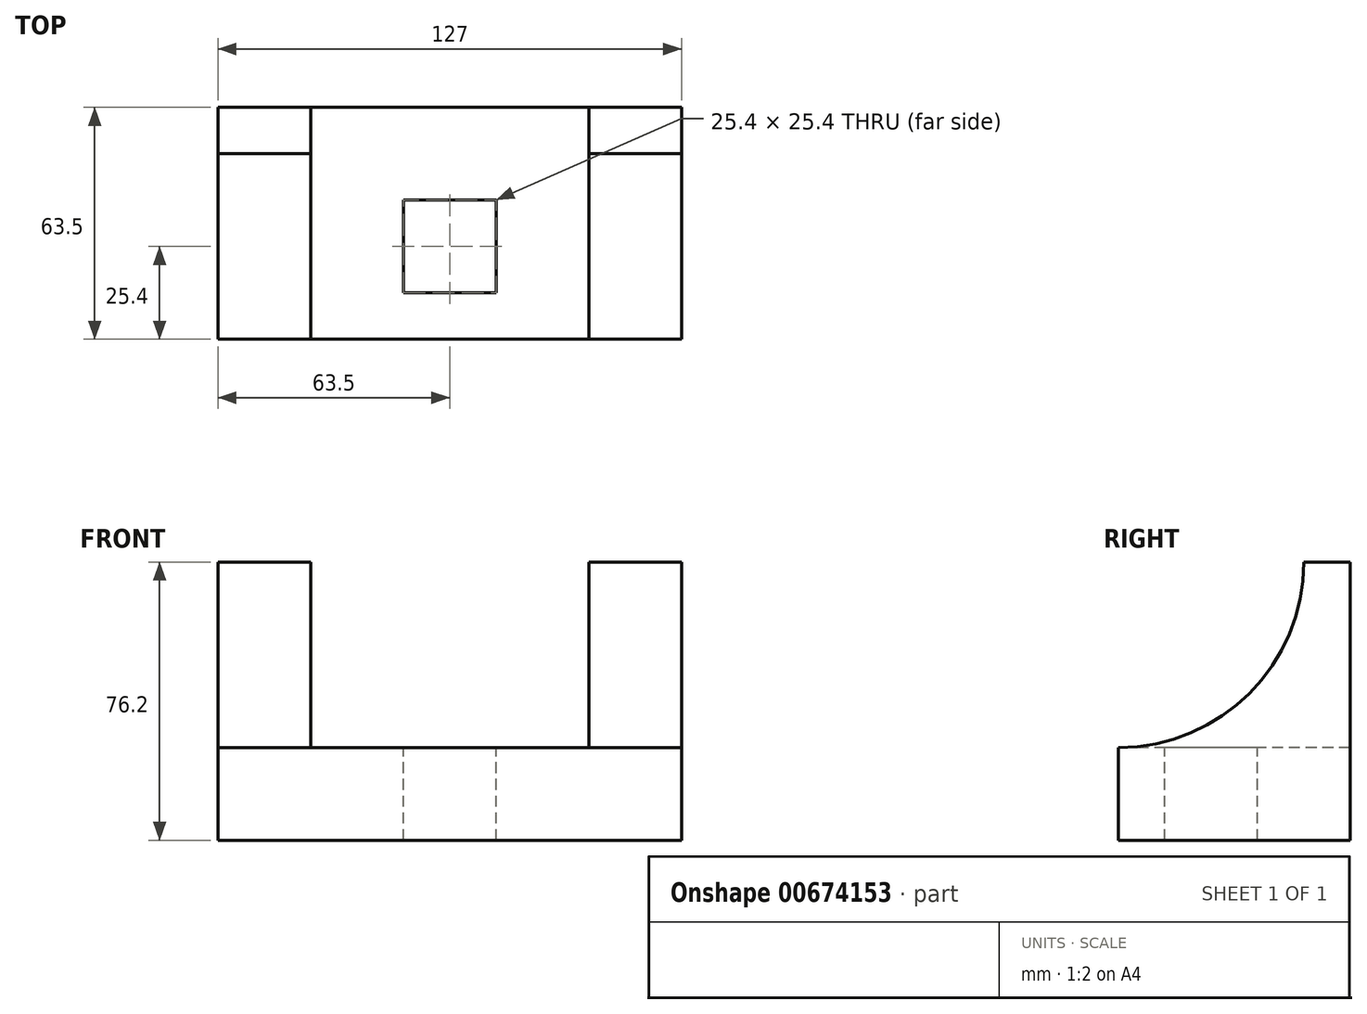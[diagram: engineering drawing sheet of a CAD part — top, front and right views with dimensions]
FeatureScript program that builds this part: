
annotation { "Feature Type Name" : "Feature", "Feature Type Description" : "" }
export const myFeature = defineFeature(function(context is Context, id is Id, definition is map)
    precondition{}
    {
        {
            var Q0;
            Q0=qCreatedBy(makeId("Front.planeOp"),FACE);
            var sketch = newSketch(context, id + "F0", { "sketchPlane" : qUnion([Q0])});
            skLineSegment(sketch, "E0.bottom", {"start": v(63.5, -38.1) * mm, "end": v(-63.5, -38.1) * mm});
            skLineSegment(sketch, "E0.top", {"start": v(63.5, 38.1) * mm, "end": v(-63.5, 38.1) * mm});
            skLineSegment(sketch, "E0.left", {"start": v(63.5, -38.1) * mm, "end": v(63.5, 38.1) * mm});
            skLineSegment(sketch, "E0.right", {"start": v(-63.5, -38.1) * mm, "end": v(-63.5, 38.1) * mm});
            skPoint(sketch, "E0.middle", {"position": v(0, 0) * mm});
            skSolve(sketch);
        }
        {
            var Q0;
            Q0 = qSketchRegion(id + "F0", true);
            extrude(context, id + "F1", {"entities" : qUnion([Q0]), "depth" : 63.5 * mm, "offsetDistance" : 25.4 * mm});
        }
        {
            var Q0;
            Q0=makeQuery(id+"F1.opExtrude","CAP_FACE",FACE,{"disambiguationData":[OSD([sQuery(id+"F0.wireOp",EDGE,"E0.bottom"),sQuery(id+"F0.wireOp",EDGE,"E0.top"),sQuery(id+"F0.wireOp",EDGE,"E0.left"),sQuery(id+"F0.wireOp",EDGE,"E0.right")])],"isStart":false});
            var sketch = newSketch(context, id + "F2", { "sketchPlane" : qUnion([Q0])});
            skLineSegment(sketch, "E1.bottom", {"start": v(-38.1, 38.1) * mm, "end": v(38.1, 38.1) * mm});
            skLineSegment(sketch, "E1.top", {"start": v(-38.1, -12.7) * mm, "end": v(38.1, -12.7) * mm});
            skLineSegment(sketch, "E1.left", {"start": v(-38.1, 38.1) * mm, "end": v(-38.1, -12.7) * mm});
            skLineSegment(sketch, "E1.right", {"start": v(38.1, 38.1) * mm, "end": v(38.1, -12.7) * mm});
            skSolve(sketch);
        }
        {
            var Q0;
            Q0 = qSketchRegion(id + "F2", true);
            extrude(context, id + "F3", {"entities" : qUnion([Q0]), "operationType" : NewBodyOperationType.REMOVE, "oppositeDirection" : true, "depth" : 63.5 * mm, "offsetDistance" : 25.4 * mm});
        }
        {
            var Q0;
            Q0=makeQuery(id+"F1.opExtrude","SWEPT_FACE",FACE,{"disambiguationData":[OSD([sQuery(id+"F0.wireOp",EDGE,"E0.right")])]});
            var sketch = newSketch(context, id + "F4", { "sketchPlane" : qUnion([Q0])});
            skCircle(sketch, "E2", {"center": v(63.5, 38.1) * mm, "radius": 50.8 * mm});
            skSolve(sketch);
        }
        {
            var Q0;
            Q0 = qSketchRegion(id + "F4", true);
            extrude(context, id + "F5", {"entities" : qUnion([Q0]), "operationType" : NewBodyOperationType.REMOVE, "oppositeDirection" : true, "depth" : 132.08 * mm, "offsetDistance" : 25.4 * mm});
        }
        {
            var Q0;
            Q0=makeQuery(id+"F3.boolean.opBoolean","COPY",FACE,{"derivedFrom":makeQuery(id+"F3.opExtrude","SWEPT_FACE",FACE,{"disambiguationData":[OSD([sQuery(id+"F2.wireOp",EDGE,"E1.top")])]})});
            var sketch = newSketch(context, id + "F6", { "sketchPlane" : qUnion([Q0])});
            skLineSegment(sketch, "E3.bottom", {"start": v(-12.7, -25.4) * mm, "end": v(12.7, -25.4) * mm});
            skLineSegment(sketch, "E3.top", {"start": v(-12.7, -50.8) * mm, "end": v(12.7, -50.8) * mm});
            skLineSegment(sketch, "E3.left", {"start": v(-12.7, -25.4) * mm, "end": v(-12.7, -50.8) * mm});
            skLineSegment(sketch, "E3.right", {"start": v(12.7, -25.4) * mm, "end": v(12.7, -50.8) * mm});
            skSolve(sketch);
        }
        {
            var Q0;
            Q0 = qSketchRegion(id + "F6", true);
            extrude(context, id + "F7", {"entities" : qUnion([Q0]), "operationType" : NewBodyOperationType.REMOVE, "oppositeDirection" : true, "depth" : 25.4 * mm, "offsetDistance" : 25.4 * mm});
        }
    });
